# Revit family: Construction_Stairs-Precision_Ladders-Super_Simplex_Disappearing_Stair-v2
name_source: partatom
category: Specialty Equipment
units: mm (PartAtom-declared; Revit-internal decimal feet)

## family parameters
Always vertical = Yes
Cut with Voids When Loaded = Yes
OmniClass Number = 23.30.70.00
OmniClass Title = Circulation and Escape
Part Type = Normal
Room Calculation Point = No
Round Connector Dimension = Use Diameter
Shared = No

## types (2) — shared parameters
Description = Super Simplex Disappearing Stairways (attic stairs or attic ladders) for roof hatch access, mezzanine access, or attic access
Door Panel Material = Metal - Precision Ladders LLC - Aluminium
Frame Material = Metal - Precision Ladders LLC - Steel
Handrail Material = Metal - Precision Ladders LLC - Aluminium
Manufacturer = Precision Ladders, LLC
Model = Super Simplex Disappearing Stairs
Product Page URL = http://www.precisionladders.com
Product data url = https://www.bimobject.com
Tread Material = Metal - Precision Ladders LLC - Aluminium
URL = http://www.precisionladders.com

## per-type parameters (varying)
| type | Box Frame |
| Box Frame | Yes |
| Angle Frame | No |

type visibility flags (boolean, named after types; folded from table):
- Box Frame: Yes: (none)
- Angle Frame: Yes: Angle Frame

## geometry (parser evidence)
native form markers: Blend x6, Sweep x18
no freeform markers — native parametric forms only
